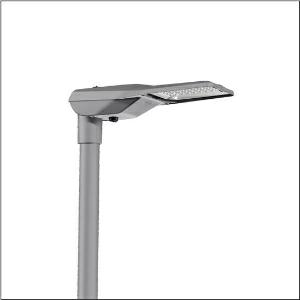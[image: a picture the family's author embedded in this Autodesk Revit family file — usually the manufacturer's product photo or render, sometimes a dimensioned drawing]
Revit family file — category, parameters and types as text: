
# Revit family: streetlight_sl_21_iq_mini___st1_0ab_5xe2m31y08jb_87eb
name_source: partatom
category: Lighting Fixtures
units: mm (PartAtom-declared; Revit-internal decimal feet)

## family parameters
Cut with Voids When Loaded = No
Host = Face
Light Source = No
Part Type = Normal
Room Calculation Point = No
Round Connector Dimension = Use Diameter
Shared = No

## types (1)
- --- (1 x LED, 9870 lm, 72.5 W, 3000K)
    Apparent Load = 73 VA
    CIE Flux Codes = 40 74 97 100 100
    Color Rendering = 70
    Color Temperature = 3000K
    Default Elevation = 1800 mm
    Description = Streetlight SL 21 iQ mini, mast luminaire, primary light control with lens, of PMMA, primary optical cover: cover, of toughened safety glass, transparent, light distribution: ST1.0aB, light emission: direct distribution, primary light characteristic: asymmetric, installation type: post-top, side-entry, LED, High Power LED, rated luminous flux: 9.870lm, luminous efficacy: 136lm/W, light colour: 730, colour temperature: 3000K, control: presetting dimming logarithmic, Street-Remote, Auto-Match, Temp-Guard, Lumen-Switch, Night-Set, Smart-Wire, Light-Fading, Desk-Remote (wireless, voltage-free reading and setting of iQ features in the workshop via application-optimized NFC function/RFID function), optimised constant luminous flux control (CLO 2.0), mains connection: 220..240V, AC, 50/60Hz, start of lifetime: 73W, end of service life: 76W, reduction: 33W, luminaire housing, of diecast aluminium, powder-coated, Siteco® metallic grey (DB 702S), corrosivity category C5 mid according to DIN EN ISO 12944, please order mast flange separately, inclination adjustable: 0°, 5°, 10°, 15°, sealing non-destructively replaceable, multi-level sealing system, length: 628mm, width: 235mm, height: 110mm, mast flange for spigot size: 42mm (side-entry): 5XC10008XM4, 60/48mm (side-entry/post-top): 5XC10108XM2, 76/60mm (side-entry/post-top): 5XC10108XM1, Smart Interface below and above, protection rating (complete): IP66, insulation class (complete): insulation class II (safety insulation), certification: CE, ENEC, ENEC+, VDE, impact resistance: IK09, permissible operating ambient temperature for outdoor applications: -40..+50°C, standard-compliant lighting for roads and squares, packaging unit: 1 piece

Light Distribution: ST1.0aB
    Height = 110 mm
    Lamp = 1 x LED
    Lamp Light Flux = 9870 lm
    Lamp Power = 72.5 W
    Lamp count = 1
    Length = 625 mm
    Luminous efficacy = 136 lm/W
    Manufacturer = Siteco
    ModVariant = No
    Model = 5XE2M31Y08JB
    Number of Poles = 1
    OnlyDefault = Yes
    Power Factor = 1
    Product Name = Streetlight SL 21 iQ mini | ST1.0aB
    Product group = mast luminaire | pylon top
    ProductGroupID = 6100
    Protection Class = Protection class II
    Protection Degree = IP 66
    RLX_Detail_Level = 1
    RLX_Emergency_Light_Flux = 0 lm
    RLX_Emergency_Type = 0
    RLX_Emergency_Type_DB = No
    RlxData = <blob elided: 92869 chars, md5=557d078f>
    Socket = socket
    Standby Power = 0 W
    System Light Flux = 9870 lm
    System Power = 73 W
    Type Comments = factory setting: luminous flux: 100 % | dim-lin: 254 | 755 mA
    Type Image = l_1003514.jpg
    URL = http://relux.com
    VarID = @adj_042255
    Voltage = 0 V
    Weight = 0.00 kg
    Width = 234 mm

## geometry (parser evidence)
native form markers: Blend x4, Sweep x11
no freeform markers — native parametric forms only
